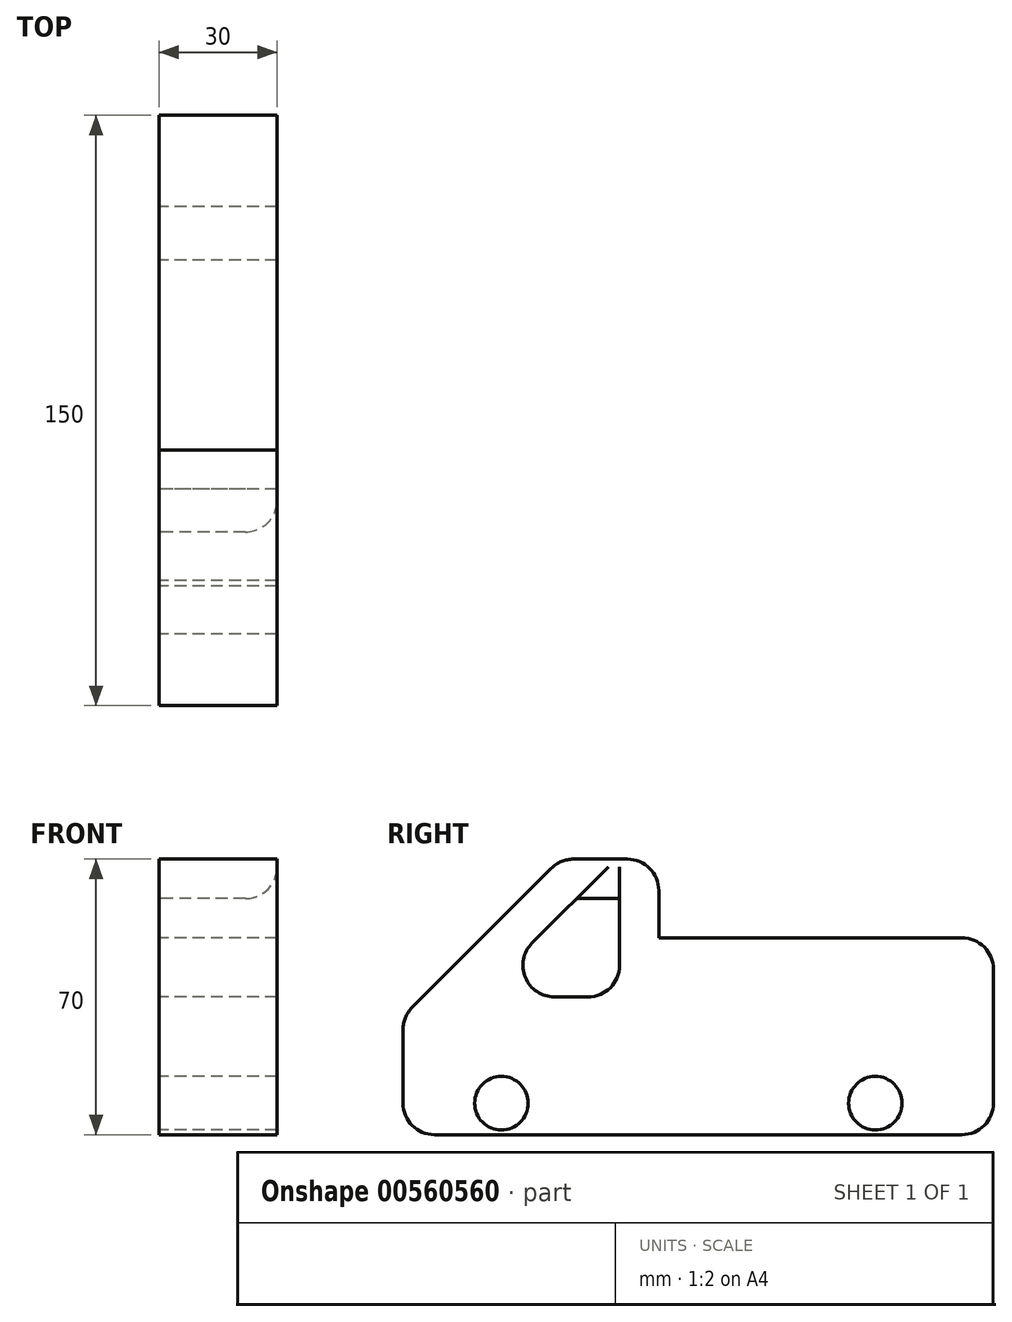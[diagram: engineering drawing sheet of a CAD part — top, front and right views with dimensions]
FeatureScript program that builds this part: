
annotation { "Feature Type Name" : "Feature", "Feature Type Description" : "" }
export const myFeature = defineFeature(function(context is Context, id is Id, definition is map)
    precondition{}
    {
        {
            var Q0;
            Q0=qCreatedBy(makeId("Right.planeOp"),FACE);
            var sketch = newSketch(context, id + "F0", { "sketchPlane" : qUnion([Q0])});
            skLineSegment(sketch, "E0", {"start": v(0, 0) * mm, "end": v(0, 30) * mm});
            skLineSegment(sketch, "E1", {"start": v(0, 30) * mm, "end": v(40, 70) * mm});
            skLineSegment(sketch, "E2", {"start": v(40, 70) * mm, "end": v(65, 70) * mm});
            skLineSegment(sketch, "E3", {"start": v(65, 70) * mm, "end": v(65, 50) * mm});
            skLineSegment(sketch, "E4", {"start": v(65, 50) * mm, "end": v(150, 50) * mm});
            skLineSegment(sketch, "E5", {"start": v(150, 50) * mm, "end": v(150, 0) * mm});
            skLineSegment(sketch, "E6", {"start": v(150, 0) * mm, "end": v(0, 0) * mm});
            skLineSegment(sketch, "E7.0", {"start": v(55, 60) * mm, "end": v(55, 35) * mm});
            skLineSegment(sketch, "E7.1", {"start": v(44.14, 60) * mm, "end": v(55, 60) * mm});
            skLineSegment(sketch, "E7.2", {"start": v(19.14, 35) * mm, "end": v(44.14, 60) * mm});
            skLineSegment(sketch, "E8", {"start": v(19.14, 35) * mm, "end": v(55, 35) * mm});
            skCircle(sketch, "E9", {"center": v(25, 8) * mm, "radius": 6.8 * mm});
            skCircle(sketch, "E10", {"center": v(120, 8) * mm, "radius": 6.8 * mm});
            skSolve(sketch);
        }
        {
            var Q0;
            Q0 = qSketchRegion(id + "F0", true);
            extrude(context, id + "F1", {"entities" : qUnion([Q0]), "endBound" : BoundingType.SYMMETRIC, "depth" : 30 * mm, "offsetDistance" : 25 * mm});
        }
        {
            var Q0;
            Q0=makeQuery(id+"F1.opExtrude","SWEPT_EDGE",EDGE,{"disambiguationData":[OSD([sQuery(id+"F0.wireOp",EDGE,"E1"),sQuery(id+"F0.wireOp",EDGE,"E2")])]});
            var Q1;
            Q1=makeQuery(id+"F1.opExtrude","SWEPT_EDGE",EDGE,{"disambiguationData":[OSD([sQuery(id+"F0.wireOp",EDGE,"E2"),sQuery(id+"F0.wireOp",EDGE,"E3")])]});
            var Q2;
            Q2=makeQuery(id+"F1.opExtrude","SWEPT_EDGE",EDGE,{"disambiguationData":[OSD([sQuery(id+"F0.wireOp",EDGE,"E4"),sQuery(id+"F0.wireOp",EDGE,"E5")])]});
            var Q3;
            Q3=makeQuery(id+"F1.opExtrude","SWEPT_EDGE",EDGE,{"disambiguationData":[OSD([sQuery(id+"F0.wireOp",EDGE,"E0"),sQuery(id+"F0.wireOp",EDGE,"E1")])]});
            var Q4;
            Q4=makeQuery(id+"F1.opExtrude","SWEPT_EDGE",EDGE,{"disambiguationData":[OSD([sQuery(id+"F0.wireOp",EDGE,"E0"),sQuery(id+"F0.wireOp",EDGE,"E6")])]});
            var Q5;
            Q5=makeQuery(id+"F1.opExtrude","SWEPT_EDGE",EDGE,{"disambiguationData":[OSD([sQuery(id+"F0.wireOp",EDGE,"E5"),sQuery(id+"F0.wireOp",EDGE,"E6")])]});
            var Q6;
            Q6=makeQuery(id+"F1.opExtrude","SWEPT_EDGE",EDGE,{"disambiguationData":[OSD([sQuery(id+"F0.wireOp",EDGE,"E7.2"),sQuery(id+"F0.wireOp",EDGE,"E8")])]});
            var Q7;
            Q7=makeQuery(id+"F1.opExtrude","CAP_EDGE",EDGE,{"disambiguationData":[OSD([sQuery(id+"F0.wireOp",EDGE,"E7.1")])],"isStart":false});
            var Q8;
            Q8=makeQuery(id+"F1.opExtrude","SWEPT_EDGE",EDGE,{"disambiguationData":[OSD([sQuery(id+"F0.wireOp",EDGE,"E7.0"),sQuery(id+"F0.wireOp",EDGE,"E8")])]});
            fillet(context, id + "F2", {"entities" : qUnion([Q0, Q1, Q2, Q3, Q4, Q5, Q6, Q7, Q8]), "radius" : 8 * mm, "tangentPropagation" : true, "allowEdgeOverflow" : false});
        }
    });
